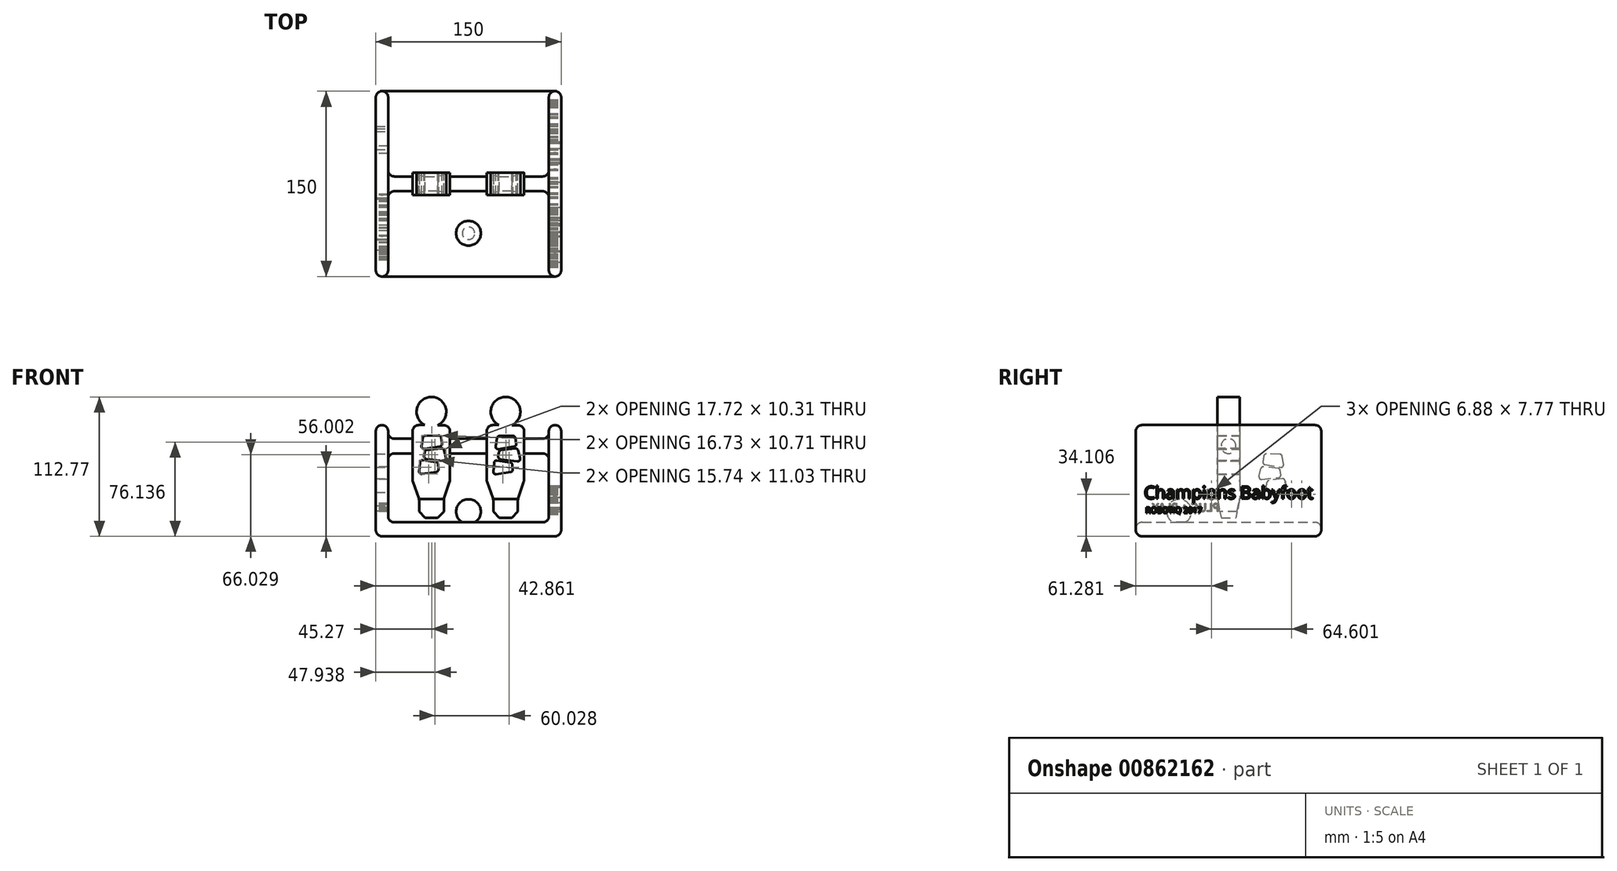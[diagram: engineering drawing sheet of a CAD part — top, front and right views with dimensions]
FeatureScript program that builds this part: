
annotation { "Feature Type Name" : "Feature", "Feature Type Description" : "" }
export const myFeature = defineFeature(function(context is Context, id is Id, definition is map)
    precondition{}
    {
        {
            var Q0;
            Q0=qCreatedBy(makeId("Front.planeOp"),FACE);
            var sketch = newSketch(context, id + "F0", { "sketchPlane" : qUnion([Q0])});
            skLineSegment(sketch, "E0.left", {"start": v(-40, 15) * mm, "end": v(-40, 0) * mm});
            skLineSegment(sketch, "E0.right", {"start": v(-20, 15) * mm, "end": v(-20, 0) * mm});
            skLineSegment(sketch, "E1", {"start": v(-45.3, 75) * mm, "end": v(-35.3, 75) * mm});
            skLineSegment(sketch, "E2", {"start": v(-25, 74.86) * mm, "end": v(-15, 74.86) * mm});
            skArc(sketch, "E3", {"start": v(-25, 74.86) * mm, "mid": v(-29.84, 97.77) * mm, "end": v(-35.3, 75) * mm});
            skLineSegment(sketch, "E4", {"start": v(-40, 0) * mm, "end": v(-30, 0) * mm});
            skLineSegment(sketch, "E5", {"start": v(-30, 0) * mm, "end": v(-20, 0) * mm});
            skLineSegment(sketch, "E6", {"start": v(-15, 74.86) * mm, "end": v(-15, 29.86) * mm});
            skLineSegment(sketch, "E7", {"start": v(-15, 29.86) * mm, "end": v(-20, 15) * mm});
            skLineSegment(sketch, "E8", {"start": v(-45.3, 75) * mm, "end": v(-45.3, 30) * mm});
            skLineSegment(sketch, "E9", {"start": v(-45.3, 30) * mm, "end": v(-40, 15) * mm});
            skLineSegment(sketch, "E10.left", {"start": v(20, 15) * mm, "end": v(20, 0) * mm});
            skLineSegment(sketch, "E10.right", {"start": v(40, 15) * mm, "end": v(40, 0) * mm});
            skLineSegment(sketch, "E11", {"start": v(14.7, 75) * mm, "end": v(24.7, 75) * mm});
            skLineSegment(sketch, "E12", {"start": v(35, 74.86) * mm, "end": v(45, 74.86) * mm});
            skArc(sketch, "E13", {"start": v(35, 74.86) * mm, "mid": v(30.16, 97.77) * mm, "end": v(24.7, 75) * mm});
            skLineSegment(sketch, "E14", {"start": v(20, 0) * mm, "end": v(30, 0) * mm});
            skLineSegment(sketch, "E15", {"start": v(30, 0) * mm, "end": v(40, 0) * mm});
            skLineSegment(sketch, "E16", {"start": v(45, 74.86) * mm, "end": v(45, 29.86) * mm});
            skLineSegment(sketch, "E17", {"start": v(45, 29.86) * mm, "end": v(40, 15) * mm});
            skLineSegment(sketch, "E18", {"start": v(14.7, 75) * mm, "end": v(14.7, 30) * mm});
            skLineSegment(sketch, "E19", {"start": v(14.7, 30) * mm, "end": v(20, 15) * mm});
            skSolve(sketch);
        }
        {
            var Q0;
            Q0=qSketchRegion(id+"F0",true);
            extrude(context, id + "F1", {"entities" : qUnion([Q0]), "endBound" : BoundingType.SYMMETRIC, "depth" : 18 * mm});
        }
        {
            var Q0;
            Q0=makeQuery(id+"F1.opExtrude","SWEPT_EDGE",EDGE,{"disambiguationData":[OSD([sQuery(id+"F0.wireOp",EDGE,"E1"),sQuery(id+"F0.wireOp",EDGE,"E8")])]});
            var Q1;
            Q1=makeQuery(id+"F1.opExtrude","SWEPT_EDGE",EDGE,{"disambiguationData":[OSD([sQuery(id+"F0.wireOp",EDGE,"E8"),sQuery(id+"F0.wireOp",EDGE,"E9")])]});
            var Q2;
            Q2=makeQuery(id+"F1.opExtrude","SWEPT_EDGE",EDGE,{"disambiguationData":[OSD([sQuery(id+"F0.wireOp",EDGE,"E0.left"),sQuery(id+"F0.wireOp",EDGE,"E9")])]});
            var Q3;
            Q3=makeQuery(id+"F1.opExtrude","SWEPT_EDGE",EDGE,{"disambiguationData":[OSD([sQuery(id+"F0.wireOp",EDGE,"E10.left"),sQuery(id+"F0.wireOp",EDGE,"E19")])]});
            var Q4;
            Q4=makeQuery(id+"F1.opExtrude","SWEPT_EDGE",EDGE,{"disambiguationData":[OSD([sQuery(id+"F0.wireOp",EDGE,"E18"),sQuery(id+"F0.wireOp",EDGE,"E19")])]});
            var Q5;
            Q5=makeQuery(id+"F1.opExtrude","SWEPT_EDGE",EDGE,{"disambiguationData":[OSD([sQuery(id+"F0.wireOp",EDGE,"E11"),sQuery(id+"F0.wireOp",EDGE,"E18")])]});
            var Q6;
            Q6=makeQuery(id+"F1.opExtrude","SWEPT_EDGE",EDGE,{"disambiguationData":[OSD([sQuery(id+"F0.wireOp",EDGE,"E2"),sQuery(id+"F0.wireOp",EDGE,"E6")])]});
            var Q7;
            Q7=makeQuery(id+"F1.opExtrude","SWEPT_EDGE",EDGE,{"disambiguationData":[OSD([sQuery(id+"F0.wireOp",EDGE,"E6"),sQuery(id+"F0.wireOp",EDGE,"E7")])]});
            var Q8;
            Q8=makeQuery(id+"F1.opExtrude","SWEPT_EDGE",EDGE,{"disambiguationData":[OSD([sQuery(id+"F0.wireOp",EDGE,"E0.right"),sQuery(id+"F0.wireOp",EDGE,"E7")])]});
            var Q9;
            Q9=makeQuery(id+"F1.opExtrude","SWEPT_EDGE",EDGE,{"disambiguationData":[OSD([sQuery(id+"F0.wireOp",EDGE,"E10.right"),sQuery(id+"F0.wireOp",EDGE,"E17")])]});
            var Q10;
            Q10=makeQuery(id+"F1.opExtrude","SWEPT_EDGE",EDGE,{"disambiguationData":[OSD([sQuery(id+"F0.wireOp",EDGE,"E16"),sQuery(id+"F0.wireOp",EDGE,"E17")])]});
            var Q11;
            Q11=makeQuery(id+"F1.opExtrude","SWEPT_EDGE",EDGE,{"disambiguationData":[OSD([sQuery(id+"F0.wireOp",EDGE,"E12"),sQuery(id+"F0.wireOp",EDGE,"E16")])]});
            fillet(context, id + "F2", {"entities" : qUnion([Q0, Q1, Q2, Q3, Q4, Q5, Q6, Q7, Q8, Q9, Q10, Q11]), "radius" : 5 * mm, "tangentPropagation" : true, "allowEdgeOverflow" : false});
        }
        {
            var Q0;
            Q0=makeQuery(id+"F1.opExtrude","SWEPT_EDGE",EDGE,{"disambiguationData":[OSD([sQuery(id+"F0.wireOp",EDGE,"E0.left"),sQuery(id+"F0.wireOp",EDGE,"E4")])]});
            var Q1;
            Q1=makeQuery(id+"F1.opExtrude","SWEPT_EDGE",EDGE,{"disambiguationData":[OSD([sQuery(id+"F0.wireOp",EDGE,"E0.right"),sQuery(id+"F0.wireOp",EDGE,"E5")])]});
            var Q2;
            Q2=makeQuery(id+"F1.opExtrude","SWEPT_EDGE",EDGE,{"disambiguationData":[OSD([sQuery(id+"F0.wireOp",EDGE,"E10.right"),sQuery(id+"F0.wireOp",EDGE,"E15")])]});
            var Q3;
            Q3=makeQuery(id+"F1.opExtrude","SWEPT_EDGE",EDGE,{"disambiguationData":[OSD([sQuery(id+"F0.wireOp",EDGE,"E10.left"),sQuery(id+"F0.wireOp",EDGE,"E14")])]});
            chamfer(context, id + "F3", {"entities" : qUnion([Q0, Q1, Q2, Q3]), "width" : 5 * mm, "tangentPropagation" : true});
        }
        {
            var Q0;
            Q0=makeQuery(id+"F1.opExtrude","CAP_EDGE",EDGE,{"disambiguationData":[OSD([sQuery(id+"F0.wireOp",EDGE,"E4"),sQuery(id+"F0.wireOp",EDGE,"E5")])],"isStart":false});
            var Q1;
            Q1=makeQuery(id+"F1.opExtrude","CAP_EDGE",EDGE,{"disambiguationData":[OSD([sQuery(id+"F0.wireOp",EDGE,"E14"),sQuery(id+"F0.wireOp",EDGE,"E15")])],"isStart":false});
            var Q2;
            Q2=makeQuery(id+"F1.opExtrude","CAP_EDGE",EDGE,{"disambiguationData":[OSD([sQuery(id+"F0.wireOp",EDGE,"E14"),sQuery(id+"F0.wireOp",EDGE,"E15")])],"isStart":true});
            var Q3;
            Q3=makeQuery(id+"F1.opExtrude","CAP_EDGE",EDGE,{"disambiguationData":[OSD([sQuery(id+"F0.wireOp",EDGE,"E4"),sQuery(id+"F0.wireOp",EDGE,"E5")])],"isStart":true});
            chamfer(context, id + "F4", {"entities" : qUnion([Q0, Q1, Q2, Q3]), "chamferType" : ChamferType.TWO_OFFSETS, "width1" : 15 * mm, "oppositeDirection" : false, "width2" : 3 * mm, "tangentPropagation" : true});
        }
        {
            var Q0;
            Q0=qCreatedBy(makeId("Right.planeOp"),FACE);
            var sketch = newSketch(context, id + "F5", { "sketchPlane" : qUnion([Q0])});
            skCircle(sketch, "E20", {"center": v(0, 58) * mm, "radius": 6 * mm});
            skSolve(sketch);
        }
        {
            var Q0;
            Q0=qSketchRegion(id+"F5",true);
            extrude(context, id + "F6", {"entities" : qUnion([Q0]), "operationType" : NewBodyOperationType.ADD, "endBound" : BoundingType.SYMMETRIC, "depth" : 150 * mm});
        }
        {
            var Q0;
            Q0=qCreatedBy(makeId("Front.planeOp"),FACE);
            cPlane(context, id + "F7", {"entities" : qUnion([Q0]), "cplaneType" : CPlaneType.OFFSET, "offset" : 40 * mm, "width" : 150 * mm, "height" : 150 * mm});
        }
        {
            var Q0;
            Q0=qCreatedBy(id+"F7.planeOp",FACE);
            var sketch = newSketch(context, id + "F8", { "sketchPlane" : qUnion([Q0])});
            skPoint(sketch, "E21", {"position": v(0, 4.98) * mm});
            skLineSegment(sketch, "E22", {"start": v(-10, 4.93) * mm, "end": v(10, 4.93) * mm});
            skArc(sketch, "E23", {"start": v(10, 4.93) * mm, "mid": v(0, 14.93) * mm, "end": v(-10, 4.93) * mm});
            skSolve(sketch);
        }
        {
            var Q0;
            Q0=qCreatedBy(makeId("Front.planeOp"),FACE);
            var sketch = newSketch(context, id + "F9", { "sketchPlane" : qUnion([Q0])});
            skLineSegment(sketch, "E24.top", {"start": v(-75, -15) * mm, "end": v(75, -15) * mm});
            skLineSegment(sketch, "E25", {"start": v(75, -15) * mm, "end": v(75, 75) * mm});
            skLineSegment(sketch, "E26", {"start": v(75, 75) * mm, "end": v(65, 75) * mm});
            skLineSegment(sketch, "E27", {"start": v(65, 75) * mm, "end": v(65, 0) * mm});
            skLineSegment(sketch, "E28", {"start": v(-65, 1.11) * mm, "end": v(-65, 75) * mm});
            skLineSegment(sketch, "E29", {"start": v(-75, -15) * mm, "end": v(-75, 75) * mm});
            skLineSegment(sketch, "E30", {"start": v(-75, 75) * mm, "end": v(-65, 75) * mm});
            skLineSegment(sketch, "E31", {"start": v(65, 0) * mm, "end": v(65, -3.72) * mm});
            skLineSegment(sketch, "E32", {"start": v(65, -3.72) * mm, "end": v(-65, -3.72) * mm});
            skLineSegment(sketch, "E33", {"start": v(-65, 1.11) * mm, "end": v(-65, -3.72) * mm});
            skSolve(sketch);
        }
        {
            var Q0;
            Q0=qSketchRegion(id+"F9",true);
            extrude(context, id + "F10", {"entities" : qUnion([Q0]), "operationType" : NewBodyOperationType.ADD, "endBound" : BoundingType.SYMMETRIC, "depth" : 150 * mm});
        }
        {
            var Q0;
            Q0=makeQuery(id+"F10.opExtrude","SWEPT_EDGE",EDGE,{"disambiguationData":[OSD([sQuery(id+"F9.wireOp",EDGE,"E29"),sQuery(id+"F9.wireOp",EDGE,"E30")])]});
            var Q1;
            Q1=makeQuery(id+"F10.opExtrude","CAP_EDGE",EDGE,{"disambiguationData":[OSD([sQuery(id+"F9.wireOp",EDGE,"E30")])],"isStart":false});
            var Q2;
            Q2=makeQuery(id+"F10.opExtrude","CAP_EDGE",EDGE,{"disambiguationData":[OSD([sQuery(id+"F9.wireOp",EDGE,"E30")])],"isStart":true});
            var Q3;
            Q3=makeQuery(id+"F10.opExtrude","SWEPT_EDGE",EDGE,{"disambiguationData":[OSD([sQuery(id+"F9.wireOp",EDGE,"E28"),sQuery(id+"F9.wireOp",EDGE,"E30")])]});
            var Q4;
            Q4=makeQuery(id+"F10.opExtrude","CAP_EDGE",EDGE,{"disambiguationData":[OSD([sQuery(id+"F9.wireOp",EDGE,"E28"),sQuery(id+"F9.wireOp",EDGE,"E33")])],"isStart":true});
            var Q5;
            Q5=makeQuery(id+"F10.opExtrude","CAP_EDGE",EDGE,{"disambiguationData":[OSD([sQuery(id+"F9.wireOp",EDGE,"E29")])],"isStart":true});
            var Q6;
            Q6=makeQuery(id+"F10.opExtrude","CAP_EDGE",EDGE,{"disambiguationData":[OSD([sQuery(id+"F9.wireOp",EDGE,"E29")])],"isStart":false});
            var Q7;
            Q7=makeQuery(id+"F10.opExtrude","CAP_EDGE",EDGE,{"disambiguationData":[OSD([sQuery(id+"F9.wireOp",EDGE,"E28"),sQuery(id+"F9.wireOp",EDGE,"E33")])],"isStart":false});
            var Q8;
            Q8=makeQuery(id+"F10.opExtrude","CAP_EDGE",EDGE,{"disambiguationData":[OSD([sQuery(id+"F9.wireOp",EDGE,"E32")])],"isStart":false});
            var Q9;
            Q9=makeQuery(id+"F10.opExtrude","CAP_EDGE",EDGE,{"disambiguationData":[OSD([sQuery(id+"F9.wireOp",EDGE,"E24.top")])],"isStart":false});
            var Q10;
            Q10=makeQuery(id+"F10.opExtrude","SWEPT_EDGE",EDGE,{"disambiguationData":[OSD([sQuery(id+"F9.wireOp",EDGE,"E24.top"),sQuery(id+"F9.wireOp",EDGE,"E29")])]});
            var Q11;
            Q11=makeQuery(id+"F10.opExtrude","CAP_EDGE",EDGE,{"disambiguationData":[OSD([sQuery(id+"F9.wireOp",EDGE,"E24.top")])],"isStart":true});
            var Q12;
            Q12=makeQuery(id+"F10.opExtrude","SWEPT_EDGE",EDGE,{"disambiguationData":[OSD([sQuery(id+"F9.wireOp",EDGE,"E24.top"),sQuery(id+"F9.wireOp",EDGE,"E25")])]});
            var Q13;
            Q13=makeQuery(id+"F10.opExtrude","CAP_EDGE",EDGE,{"disambiguationData":[OSD([sQuery(id+"F9.wireOp",EDGE,"E25")])],"isStart":false});
            var Q14;
            Q14=makeQuery(id+"F10.opExtrude","CAP_EDGE",EDGE,{"disambiguationData":[OSD([sQuery(id+"F9.wireOp",EDGE,"E27"),sQuery(id+"F9.wireOp",EDGE,"E31")])],"isStart":false});
            var Q15;
            Q15=makeQuery(id+"F10.opExtrude","CAP_EDGE",EDGE,{"disambiguationData":[OSD([sQuery(id+"F9.wireOp",EDGE,"E25")])],"isStart":true});
            var Q16;
            Q16=makeQuery(id+"F10.opExtrude","CAP_EDGE",EDGE,{"disambiguationData":[OSD([sQuery(id+"F9.wireOp",EDGE,"E27"),sQuery(id+"F9.wireOp",EDGE,"E31")])],"isStart":true});
            var Q17;
            Q17=makeQuery(id+"F10.opExtrude","CAP_EDGE",EDGE,{"disambiguationData":[OSD([sQuery(id+"F9.wireOp",EDGE,"E32")])],"isStart":true});
            var Q18;
            Q18=makeQuery(id+"F10.opExtrude","CAP_EDGE",EDGE,{"disambiguationData":[OSD([sQuery(id+"F9.wireOp",EDGE,"E26")])],"isStart":true});
            var Q19;
            Q19=makeQuery(id+"F10.opExtrude","SWEPT_EDGE",EDGE,{"disambiguationData":[OSD([sQuery(id+"F9.wireOp",EDGE,"E25"),sQuery(id+"F9.wireOp",EDGE,"E26")])]});
            var Q20;
            Q20=makeQuery(id+"F10.opExtrude","SWEPT_EDGE",EDGE,{"disambiguationData":[OSD([sQuery(id+"F9.wireOp",EDGE,"E26"),sQuery(id+"F9.wireOp",EDGE,"E27")])]});
            var Q21;
            Q21=makeQuery(id+"F10.opExtrude","SWEPT_EDGE",EDGE,{"disambiguationData":[OSD([sQuery(id+"F9.wireOp",EDGE,"E32"),sQuery(id+"F9.wireOp",EDGE,"E33")])]});
            var Q22;
            Q22=makeQuery(id+"F10.opExtrude","SWEPT_FACE",FACE,{"disambiguationData":[OSD([sQuery(id+"F9.wireOp",EDGE,"E27"),sQuery(id+"F9.wireOp",EDGE,"E31")])]});
            var Q23;
            Q23=makeQuery(id+"F10.opExtrude","CAP_EDGE",EDGE,{"disambiguationData":[OSD([sQuery(id+"F9.wireOp",EDGE,"E26")])],"isStart":false});
            var Q24;
            {var subQ0=sQuery(id+"F5.wireOp",EDGE,"E20");Q24=makeQuery(id+"F10.boolean.opBoolean","INTERSECT",EDGE,{"derivedFrom":[makeQuery(id+"F6.boolean.opBoolean","SPLIT",FACE,{"disambiguationData":[TD([makeQuery(id+"F1.opExtrude","SWEPT_FACE",FACE,{"disambiguationData":[OSD([sQuery(id+"F0.wireOp",EDGE,"E8")])]})])],"derivedFrom":makeQuery(id+"F6.opExtrude","SWEPT_FACE",FACE,{"disambiguationData":[OSD([subQ0])]})}),makeQuery(id+"F10.opExtrude","SWEPT_FACE",FACE,{"disambiguationData":[OSD([sQuery(id+"F9.wireOp",EDGE,"E28"),sQuery(id+"F9.wireOp",EDGE,"E33")])]})]});}
            fillet(context, id + "F11", {"entities" : qUnion([Q0, Q1, Q2, Q3, Q4, Q5, Q6, Q7, Q8, Q9, Q10, Q11, Q12, Q13, Q14, Q15, Q16, Q17, Q18, Q19, Q20, Q21, Q22, Q23, Q24]), "radius" : 5 * mm, "tangentPropagation" : true, "allowEdgeOverflow" : false});
        }
        {
            var Q0;
            Q0=makeQuery(id+"F10.boolean.opBoolean","MERGE",FACE,{"derivedFrom":[makeQuery(id+"F6.opExtrude","CAP_FACE",FACE,{"disambiguationData":[OSD([sQuery(id+"F5.wireOp",EDGE,"E20")])],"isStart":false}),makeQuery(id+"F10.opExtrude","SWEPT_FACE",FACE,{"disambiguationData":[OSD([sQuery(id+"F9.wireOp",EDGE,"E25")])]})]});
            var sketch = newSketch(context, id + "F12", { "sketchPlane" : qUnion([Q0])});
            skText(sketch, "E34", { "text": "Champions Babyfoot", "fontName": "OpenSans-Regular.ttf"});
            skText(sketch, "E35", { "text": "ROBOTIQ 2017", "fontName": "OpenSans-Regular.ttf"});
            const initialGuessF12  = {"E34": [-0.0683, 0.01536, 1, 0, 0.01008], "E35": [-0.06708, 0.00377, 1, 0, 0.0047]};
            skSetInitialGuess(sketch, initialGuessF12);
            skSolve(sketch);
        }
        {
            var Q0;
            Q0=qSketchRegion(id+"F12",true);
            extrude(context, id + "F13", {"entities" : qUnion([Q0]), "operationType" : NewBodyOperationType.REMOVE, "oppositeDirection" : true, "depth" : 25 * mm});
        }
        {
            var Q0;
            Q0=makeQuery(id+"F10.boolean.opBoolean","MERGE",FACE,{"derivedFrom":[makeQuery(id+"F6.opExtrude","CAP_FACE",FACE,{"disambiguationData":[OSD([sQuery(id+"F5.wireOp",EDGE,"E20")])],"isStart":true}),makeQuery(id+"F10.opExtrude","SWEPT_FACE",FACE,{"disambiguationData":[OSD([sQuery(id+"F9.wireOp",EDGE,"E29")])]})]});
            var sketch = newSketch(context, id + "F14", { "sketchPlane" : qUnion([Q0])});
            skLineSegment(sketch, "E36", {"start": v(-43.16, 51.43) * mm, "end": v(-44.96, 40.45) * mm});
            skLineSegment(sketch, "E37", {"start": v(-44.96, 40.45) * mm, "end": v(-27.5, 43.23) * mm});
            skLineSegment(sketch, "E38", {"start": v(-27.5, 43.23) * mm, "end": v(-28.84, 51.6) * mm});
            skLineSegment(sketch, "E39", {"start": v(-28.84, 51.6) * mm, "end": v(-43.16, 51.43) * mm});
            skLineSegment(sketch, "E40", {"start": v(-41.54, 39.83) * mm, "end": v(-42.66, 32.89) * mm});
            skLineSegment(sketch, "E41", {"start": v(-42.66, 32.89) * mm, "end": v(-24, 30.61) * mm});
            skLineSegment(sketch, "E42", {"start": v(-26.68, 41.46) * mm, "end": v(-41.54, 39.83) * mm});
            skLineSegment(sketch, "E43", {"start": v(-26.68, 41.46) * mm, "end": v(-24, 30.61) * mm});
            skLineSegment(sketch, "E44", {"start": v(-45.62, 31.87) * mm, "end": v(-46.67, 20.24) * mm});
            skLineSegment(sketch, "E45", {"start": v(-46.67, 20.24) * mm, "end": v(-30.53, 22.48) * mm});
            skLineSegment(sketch, "E46", {"start": v(-31.2, 29.92) * mm, "end": v(-45.62, 31.87) * mm});
            skLineSegment(sketch, "E47", {"start": v(-31.2, 29.92) * mm, "end": v(-30.53, 22.48) * mm});
            skSolve(sketch);
        }
        {
            var Q0;
            Q0=makeQuery(id+"F14.imprint","IMPRINT",FACE,{"disambiguationData":[TD([[makeQuery(id+"F14.imprint","IMPRINT",EDGE,{"derivedFrom":sQuery(id+"F14.wireOp",EDGE,"E36")}),1.0]])]});
            var Q1;
            Q1=makeQuery(id+"F14.imprint","IMPRINT",FACE,{"disambiguationData":[TD([[makeQuery(id+"F14.imprint","IMPRINT",EDGE,{"derivedFrom":sQuery(id+"F14.wireOp",EDGE,"E40")}),1.0]])]});
            var Q2;
            Q2=makeQuery(id+"F14.imprint","IMPRINT",FACE,{"disambiguationData":[TD([[makeQuery(id+"F14.imprint","IMPRINT",EDGE,{"derivedFrom":sQuery(id+"F14.wireOp",EDGE,"E44")}),1.0]])]});
            extrude(context, id + "F15", {"entities" : qUnion([Q0, Q1, Q2]), "operationType" : NewBodyOperationType.REMOVE, "oppositeDirection" : true, "depth" : 25 * mm});
        }
        {
            var Q0;
            Q0=makeQuery(id+"F15.boolean.opBoolean","COPY",EDGE,{"derivedFrom":makeQuery(id+"F15.opExtrude","SWEPT_EDGE",EDGE,{"disambiguationData":[OSD([sQuery(id+"F14.wireOp",EDGE,"E41"),sQuery(id+"F14.wireOp",EDGE,"E43")])]})});
            var Q1;
            Q1=makeQuery(id+"F15.boolean.opBoolean","COPY",EDGE,{"derivedFrom":makeQuery(id+"F15.opExtrude","SWEPT_EDGE",EDGE,{"disambiguationData":[OSD([sQuery(id+"F14.wireOp",EDGE,"E42"),sQuery(id+"F14.wireOp",EDGE,"E43")])]})});
            var Q2;
            Q2=makeQuery(id+"F15.boolean.opBoolean","COPY",EDGE,{"derivedFrom":makeQuery(id+"F15.opExtrude","SWEPT_EDGE",EDGE,{"disambiguationData":[OSD([sQuery(id+"F14.wireOp",EDGE,"E40"),sQuery(id+"F14.wireOp",EDGE,"E41")])]})});
            var Q3;
            Q3=makeQuery(id+"F15.boolean.opBoolean","COPY",EDGE,{"derivedFrom":makeQuery(id+"F15.opExtrude","SWEPT_EDGE",EDGE,{"disambiguationData":[OSD([sQuery(id+"F14.wireOp",EDGE,"E40"),sQuery(id+"F14.wireOp",EDGE,"E42")])]})});
            var Q4;
            Q4=makeQuery(id+"F15.boolean.opBoolean","COPY",EDGE,{"derivedFrom":makeQuery(id+"F15.opExtrude","SWEPT_EDGE",EDGE,{"disambiguationData":[OSD([sQuery(id+"F14.wireOp",EDGE,"E44"),sQuery(id+"F14.wireOp",EDGE,"E46")])]})});
            var Q5;
            Q5=makeQuery(id+"F15.boolean.opBoolean","COPY",EDGE,{"derivedFrom":makeQuery(id+"F15.opExtrude","SWEPT_EDGE",EDGE,{"disambiguationData":[OSD([sQuery(id+"F14.wireOp",EDGE,"E46"),sQuery(id+"F14.wireOp",EDGE,"E47")])]})});
            var Q6;
            Q6=makeQuery(id+"F15.boolean.opBoolean","COPY",EDGE,{"derivedFrom":makeQuery(id+"F15.opExtrude","SWEPT_EDGE",EDGE,{"disambiguationData":[OSD([sQuery(id+"F14.wireOp",EDGE,"E45"),sQuery(id+"F14.wireOp",EDGE,"E47")])]})});
            var Q7;
            Q7=makeQuery(id+"F15.boolean.opBoolean","COPY",EDGE,{"derivedFrom":makeQuery(id+"F15.opExtrude","SWEPT_EDGE",EDGE,{"disambiguationData":[OSD([sQuery(id+"F14.wireOp",EDGE,"E44"),sQuery(id+"F14.wireOp",EDGE,"E45")])]})});
            var Q8;
            Q8=makeQuery(id+"F15.boolean.opBoolean","COPY",EDGE,{"derivedFrom":makeQuery(id+"F15.opExtrude","SWEPT_EDGE",EDGE,{"disambiguationData":[OSD([sQuery(id+"F14.wireOp",EDGE,"E37"),sQuery(id+"F14.wireOp",EDGE,"E38")])]})});
            var Q9;
            Q9=makeQuery(id+"F15.boolean.opBoolean","COPY",EDGE,{"derivedFrom":makeQuery(id+"F15.opExtrude","SWEPT_EDGE",EDGE,{"disambiguationData":[OSD([sQuery(id+"F14.wireOp",EDGE,"E38"),sQuery(id+"F14.wireOp",EDGE,"E39")])]})});
            var Q10;
            Q10=makeQuery(id+"F15.boolean.opBoolean","COPY",EDGE,{"derivedFrom":makeQuery(id+"F15.opExtrude","SWEPT_EDGE",EDGE,{"disambiguationData":[OSD([sQuery(id+"F14.wireOp",EDGE,"E36"),sQuery(id+"F14.wireOp",EDGE,"E37")])]})});
            var Q11;
            Q11=makeQuery(id+"F15.boolean.opBoolean","COPY",EDGE,{"derivedFrom":makeQuery(id+"F15.opExtrude","SWEPT_EDGE",EDGE,{"disambiguationData":[OSD([sQuery(id+"F14.wireOp",EDGE,"E36"),sQuery(id+"F14.wireOp",EDGE,"E39")])]})});
            fillet(context, id + "F16", {"entities" : qUnion([Q0, Q1, Q2, Q3, Q4, Q5, Q6, Q7, Q8, Q9, Q10, Q11]), "radius" : 2 * mm, "tangentPropagation" : true, "allowEdgeOverflow" : false});
        }
        {
            var Q0;
            Q0=makeQuery(id+"F1.opExtrude","CAP_FACE",FACE,{"disambiguationData":[OSD([sQuery(id+"F0.wireOp",EDGE,"E0.left"),sQuery(id+"F0.wireOp",EDGE,"E0.right"),sQuery(id+"F0.wireOp",EDGE,"E1"),sQuery(id+"F0.wireOp",EDGE,"E2"),sQuery(id+"F0.wireOp",EDGE,"E3"),sQuery(id+"F0.wireOp",EDGE,"E4"),sQuery(id+"F0.wireOp",EDGE,"E5"),sQuery(id+"F0.wireOp",EDGE,"E6"),sQuery(id+"F0.wireOp",EDGE,"E7"),sQuery(id+"F0.wireOp",EDGE,"E8"),sQuery(id+"F0.wireOp",EDGE,"E9")])],"isStart":false});
            var sketch = newSketch(context, id + "F17", { "sketchPlane" : qUnion([Q0])});
            skLineSegment(sketch, "E48", {"start": v(-36.73, 66.34) * mm, "end": v(-38.52, 55.37) * mm});
            skLineSegment(sketch, "E49", {"start": v(-38.52, 55.37) * mm, "end": v(-21.07, 58.15) * mm});
            skLineSegment(sketch, "E50", {"start": v(-21.07, 58.15) * mm, "end": v(-22.4, 66.51) * mm});
            skLineSegment(sketch, "E51", {"start": v(-22.4, 66.51) * mm, "end": v(-36.73, 66.34) * mm});
            skLineSegment(sketch, "E52", {"start": v(-35.11, 54.74) * mm, "end": v(-36.23, 47.8) * mm});
            skLineSegment(sketch, "E53", {"start": v(-36.23, 47.8) * mm, "end": v(-17.56, 45.52) * mm});
            skLineSegment(sketch, "E54", {"start": v(-20.25, 56.37) * mm, "end": v(-35.11, 54.74) * mm});
            skLineSegment(sketch, "E55", {"start": v(-20.25, 56.37) * mm, "end": v(-17.56, 45.52) * mm});
            skLineSegment(sketch, "E56", {"start": v(-39.18, 46.78) * mm, "end": v(-40.24, 35.15) * mm});
            skLineSegment(sketch, "E57", {"start": v(-40.24, 35.15) * mm, "end": v(-24.1, 37.4) * mm});
            skLineSegment(sketch, "E58", {"start": v(-24.78, 44.83) * mm, "end": v(-39.18, 46.78) * mm});
            skLineSegment(sketch, "E59", {"start": v(-24.78, 44.83) * mm, "end": v(-24.1, 37.4) * mm});
            skLineSegment(sketch, "E60", {"start": v(23.3, 66.12) * mm, "end": v(21.5, 55.15) * mm});
            skLineSegment(sketch, "E61", {"start": v(21.5, 55.15) * mm, "end": v(38.96, 57.93) * mm});
            skLineSegment(sketch, "E62", {"start": v(38.96, 57.93) * mm, "end": v(37.62, 66.3) * mm});
            skLineSegment(sketch, "E63", {"start": v(37.62, 66.3) * mm, "end": v(23.3, 66.12) * mm});
            skLineSegment(sketch, "E64", {"start": v(24.92, 54.52) * mm, "end": v(23.8, 47.58) * mm});
            skLineSegment(sketch, "E65", {"start": v(23.8, 47.58) * mm, "end": v(42.47, 45.3) * mm});
            skLineSegment(sketch, "E66", {"start": v(39.78, 56.15) * mm, "end": v(24.92, 54.52) * mm});
            skLineSegment(sketch, "E67", {"start": v(39.78, 56.15) * mm, "end": v(42.47, 45.3) * mm});
            skLineSegment(sketch, "E68", {"start": v(20.84, 46.56) * mm, "end": v(19.8, 34.93) * mm});
            skLineSegment(sketch, "E69", {"start": v(19.8, 34.93) * mm, "end": v(35.93, 37.17) * mm});
            skLineSegment(sketch, "E70", {"start": v(35.25, 44.6) * mm, "end": v(20.84, 46.56) * mm});
            skLineSegment(sketch, "E71", {"start": v(35.25, 44.6) * mm, "end": v(35.93, 37.17) * mm});
            skSolve(sketch);
        }
        {
            var Q0;
            Q0=qSketchRegion(id+"F17",true);
            extrude(context, id + "F18", {"entities" : qUnion([Q0]), "operationType" : NewBodyOperationType.REMOVE, "oppositeDirection" : true, "depth" : 25 * mm});
        }
        {
            var Q0;
            Q0=makeQuery(id+"F18.boolean.opBoolean","COPY",EDGE,{"derivedFrom":makeQuery(id+"F18.opExtrude","SWEPT_EDGE",EDGE,{"disambiguationData":[OSD([sQuery(id+"F17.wireOp",EDGE,"E48"),sQuery(id+"F17.wireOp",EDGE,"E51")])]})});
            var Q1;
            Q1=makeQuery(id+"F18.boolean.opBoolean","COPY",EDGE,{"derivedFrom":makeQuery(id+"F18.opExtrude","SWEPT_EDGE",EDGE,{"disambiguationData":[OSD([sQuery(id+"F17.wireOp",EDGE,"E52"),sQuery(id+"F17.wireOp",EDGE,"E54")])]})});
            var Q2;
            Q2=makeQuery(id+"F18.boolean.opBoolean","COPY",EDGE,{"derivedFrom":makeQuery(id+"F18.opExtrude","SWEPT_EDGE",EDGE,{"disambiguationData":[OSD([sQuery(id+"F17.wireOp",EDGE,"E56"),sQuery(id+"F17.wireOp",EDGE,"E58")])]})});
            var Q3;
            Q3=makeQuery(id+"F18.boolean.opBoolean","COPY",EDGE,{"derivedFrom":makeQuery(id+"F18.opExtrude","SWEPT_EDGE",EDGE,{"disambiguationData":[OSD([sQuery(id+"F17.wireOp",EDGE,"E50"),sQuery(id+"F17.wireOp",EDGE,"E51")])]})});
            var Q4;
            Q4=makeQuery(id+"F18.boolean.opBoolean","COPY",EDGE,{"derivedFrom":makeQuery(id+"F18.opExtrude","SWEPT_EDGE",EDGE,{"disambiguationData":[OSD([sQuery(id+"F17.wireOp",EDGE,"E54"),sQuery(id+"F17.wireOp",EDGE,"E55")])]})});
            var Q5;
            Q5=makeQuery(id+"F18.boolean.opBoolean","COPY",EDGE,{"derivedFrom":makeQuery(id+"F18.opExtrude","SWEPT_EDGE",EDGE,{"disambiguationData":[OSD([sQuery(id+"F17.wireOp",EDGE,"E58"),sQuery(id+"F17.wireOp",EDGE,"E59")])]})});
            var Q6;
            Q6=makeQuery(id+"F18.boolean.opBoolean","COPY",EDGE,{"derivedFrom":makeQuery(id+"F18.opExtrude","SWEPT_EDGE",EDGE,{"disambiguationData":[OSD([sQuery(id+"F17.wireOp",EDGE,"E70"),sQuery(id+"F17.wireOp",EDGE,"E71")])]})});
            var Q7;
            Q7=makeQuery(id+"F18.boolean.opBoolean","COPY",EDGE,{"derivedFrom":makeQuery(id+"F18.opExtrude","SWEPT_EDGE",EDGE,{"disambiguationData":[OSD([sQuery(id+"F17.wireOp",EDGE,"E66"),sQuery(id+"F17.wireOp",EDGE,"E67")])]})});
            var Q8;
            Q8=makeQuery(id+"F18.boolean.opBoolean","COPY",EDGE,{"derivedFrom":makeQuery(id+"F18.opExtrude","SWEPT_EDGE",EDGE,{"disambiguationData":[OSD([sQuery(id+"F17.wireOp",EDGE,"E62"),sQuery(id+"F17.wireOp",EDGE,"E63")])]})});
            var Q9;
            Q9=makeQuery(id+"F18.boolean.opBoolean","COPY",EDGE,{"derivedFrom":makeQuery(id+"F18.opExtrude","SWEPT_EDGE",EDGE,{"disambiguationData":[OSD([sQuery(id+"F17.wireOp",EDGE,"E68"),sQuery(id+"F17.wireOp",EDGE,"E70")])]})});
            var Q10;
            Q10=makeQuery(id+"F18.boolean.opBoolean","COPY",EDGE,{"derivedFrom":makeQuery(id+"F18.opExtrude","SWEPT_EDGE",EDGE,{"disambiguationData":[OSD([sQuery(id+"F17.wireOp",EDGE,"E64"),sQuery(id+"F17.wireOp",EDGE,"E66")])]})});
            var Q11;
            Q11=makeQuery(id+"F18.boolean.opBoolean","COPY",EDGE,{"derivedFrom":makeQuery(id+"F18.opExtrude","SWEPT_EDGE",EDGE,{"disambiguationData":[OSD([sQuery(id+"F17.wireOp",EDGE,"E60"),sQuery(id+"F17.wireOp",EDGE,"E63")])]})});
            var Q12;
            Q12=makeQuery(id+"F18.boolean.opBoolean","COPY",EDGE,{"derivedFrom":makeQuery(id+"F18.opExtrude","SWEPT_EDGE",EDGE,{"disambiguationData":[OSD([sQuery(id+"F17.wireOp",EDGE,"E68"),sQuery(id+"F17.wireOp",EDGE,"E69")])]})});
            var Q13;
            Q13=makeQuery(id+"F18.boolean.opBoolean","COPY",EDGE,{"derivedFrom":makeQuery(id+"F18.opExtrude","SWEPT_EDGE",EDGE,{"disambiguationData":[OSD([sQuery(id+"F17.wireOp",EDGE,"E64"),sQuery(id+"F17.wireOp",EDGE,"E65")])]})});
            var Q14;
            Q14=makeQuery(id+"F18.boolean.opBoolean","COPY",EDGE,{"derivedFrom":makeQuery(id+"F18.opExtrude","SWEPT_EDGE",EDGE,{"disambiguationData":[OSD([sQuery(id+"F17.wireOp",EDGE,"E60"),sQuery(id+"F17.wireOp",EDGE,"E61")])]})});
            var Q15;
            Q15=makeQuery(id+"F18.boolean.opBoolean","COPY",EDGE,{"derivedFrom":makeQuery(id+"F18.opExtrude","SWEPT_EDGE",EDGE,{"disambiguationData":[OSD([sQuery(id+"F17.wireOp",EDGE,"E52"),sQuery(id+"F17.wireOp",EDGE,"E53")])]})});
            var Q16;
            Q16=makeQuery(id+"F18.boolean.opBoolean","COPY",EDGE,{"derivedFrom":makeQuery(id+"F18.opExtrude","SWEPT_EDGE",EDGE,{"disambiguationData":[OSD([sQuery(id+"F17.wireOp",EDGE,"E56"),sQuery(id+"F17.wireOp",EDGE,"E57")])]})});
            var Q17;
            Q17=makeQuery(id+"F18.boolean.opBoolean","COPY",EDGE,{"derivedFrom":makeQuery(id+"F18.opExtrude","SWEPT_EDGE",EDGE,{"disambiguationData":[OSD([sQuery(id+"F17.wireOp",EDGE,"E48"),sQuery(id+"F17.wireOp",EDGE,"E49")])]})});
            var Q18;
            Q18=makeQuery(id+"F18.boolean.opBoolean","COPY",EDGE,{"derivedFrom":makeQuery(id+"F18.opExtrude","SWEPT_EDGE",EDGE,{"disambiguationData":[OSD([sQuery(id+"F17.wireOp",EDGE,"E49"),sQuery(id+"F17.wireOp",EDGE,"E50")])]})});
            var Q19;
            Q19=makeQuery(id+"F18.boolean.opBoolean","COPY",EDGE,{"derivedFrom":makeQuery(id+"F18.opExtrude","SWEPT_EDGE",EDGE,{"disambiguationData":[OSD([sQuery(id+"F17.wireOp",EDGE,"E53"),sQuery(id+"F17.wireOp",EDGE,"E55")])]})});
            var Q20;
            Q20=makeQuery(id+"F18.boolean.opBoolean","COPY",EDGE,{"derivedFrom":makeQuery(id+"F18.opExtrude","SWEPT_EDGE",EDGE,{"disambiguationData":[OSD([sQuery(id+"F17.wireOp",EDGE,"E57"),sQuery(id+"F17.wireOp",EDGE,"E59")])]})});
            var Q21;
            Q21=makeQuery(id+"F18.boolean.opBoolean","COPY",EDGE,{"derivedFrom":makeQuery(id+"F18.opExtrude","SWEPT_EDGE",EDGE,{"disambiguationData":[OSD([sQuery(id+"F17.wireOp",EDGE,"E69"),sQuery(id+"F17.wireOp",EDGE,"E71")])]})});
            var Q22;
            Q22=makeQuery(id+"F18.boolean.opBoolean","COPY",EDGE,{"derivedFrom":makeQuery(id+"F18.opExtrude","SWEPT_EDGE",EDGE,{"disambiguationData":[OSD([sQuery(id+"F17.wireOp",EDGE,"E65"),sQuery(id+"F17.wireOp",EDGE,"E67")])]})});
            var Q23;
            Q23=makeQuery(id+"F18.boolean.opBoolean","COPY",EDGE,{"derivedFrom":makeQuery(id+"F18.opExtrude","SWEPT_EDGE",EDGE,{"disambiguationData":[OSD([sQuery(id+"F17.wireOp",EDGE,"E61"),sQuery(id+"F17.wireOp",EDGE,"E62")])]})});
            fillet(context, id + "F19", {"entities" : qUnion([Q0, Q1, Q2, Q3, Q4, Q5, Q6, Q7, Q8, Q9, Q10, Q11, Q12, Q13, Q14, Q15, Q16, Q17, Q18, Q19, Q20, Q21, Q22, Q23]), "radius" : 2 * mm, "tangentPropagation" : true, "allowEdgeOverflow" : false});
        }
        {
            var Q0;
            Q0=makeQuery(id+"F10.boolean.opBoolean","MERGE",FACE,{"derivedFrom":[makeQuery(id+"F6.opExtrude","CAP_FACE",FACE,{"disambiguationData":[OSD([sQuery(id+"F5.wireOp",EDGE,"E20")])],"isStart":true}),makeQuery(id+"F10.opExtrude","SWEPT_FACE",FACE,{"disambiguationData":[OSD([sQuery(id+"F9.wireOp",EDGE,"E29")])]})]});
            var sketch = newSketch(context, id + "F20", { "sketchPlane" : qUnion([Q0])});
            skText(sketch, "E72", { "text": "PLUG + PLAY", "fontName": "OpenSans-Regular.ttf"});
            const initialGuessF20  = {"E72": [0.00746, 0.00511, 1, 0, 0.00653]};
            skSetInitialGuess(sketch, initialGuessF20);
            skSolve(sketch);
        }
        {
            var Q0;
            Q0=qSketchRegion(id+"F20",true);
            extrude(context, id + "F21", {"entities" : qUnion([Q0]), "operationType" : NewBodyOperationType.REMOVE, "oppositeDirection" : true, "depth" : 25 * mm});
        }
        {
            var Q0;
            Q0=makeQuery(id+"F8.imprint","IMPRINT",FACE,{"disambiguationData":[TD([[makeQuery(id+"F8.imprint","IMPRINT",EDGE,{"derivedFrom":sQuery(id+"F8.wireOp",EDGE,"E22")}),1.0]])]});
            var Q1;
            Q1=sQuery(id+"F8.wireOp",EDGE,"E23");
            var Q2;
            Q2=sQuery(id+"F8.wireOp",EDGE,"E22");
            revolve(context, id + "F22", {"operationType" : NewBodyOperationType.ADD, "entities" : qUnion([Q0]), "surfaceEntities" : qUnion([Q1]), "axis" : qUnion([Q2]), "revolveType" : RevolveType.FULL});
        }
        {
            var Q0;
            {var subQ1=sQuery(id+"F9.wireOp",EDGE,"E25");Q0=makeQuery(id+"F13.boolean.opBoolean","SPLIT",FACE,{"disambiguationData":[TD([makeQuery(id+"F13.opExtrude","SWEPT_FACE",FACE,{"disambiguationData":[OSD([sQuery(id+"F12.wireOp",EDGE,"E34.sketch_text.stroke-0")])]})])],"derivedFrom":makeQuery(id+"F10.boolean.opBoolean","MERGE",FACE,{"derivedFrom":[makeQuery(id+"F6.opExtrude","CAP_FACE",FACE,{"disambiguationData":[OSD([sQuery(id+"F5.wireOp",EDGE,"E20")])],"isStart":false}),makeQuery(id+"F10.opExtrude","SWEPT_FACE",FACE,{"disambiguationData":[OSD([subQ1])]})]})});}
            cPlane(context, id + "F23", {"entities" : qUnion([Q0]), "cplaneType" : CPlaneType.OFFSET, "offset" : 5 * mm, "oppositeDirection" : true, "width" : 150 * mm, "height" : 150 * mm});
        }
        {
            var Q0;
            Q0=qCreatedBy(id+"F23.planeOp",FACE);
            var sketch = newSketch(context, id + "F24", { "sketchPlane" : qUnion([Q0])});
            skLineSegment(sketch, "E73.bottom", {"start": v(-51, 18.05) * mm, "end": v(-42.89, 18.05) * mm});
            skLineSegment(sketch, "E73.top", {"start": v(-51, 17.68) * mm, "end": v(-42.89, 17.68) * mm});
            skLineSegment(sketch, "E73.left", {"start": v(-51, 18.05) * mm, "end": v(-51, 17.68) * mm});
            skLineSegment(sketch, "E73.right", {"start": v(-42.89, 18.05) * mm, "end": v(-42.89, 17.68) * mm});
            skLineSegment(sketch, "E74.bottom", {"start": v(-29.8, 19.6) * mm, "end": v(-21.69, 19.6) * mm});
            skLineSegment(sketch, "E74.top", {"start": v(-29.8, 19.24) * mm, "end": v(-21.69, 19.24) * mm});
            skLineSegment(sketch, "E74.left", {"start": v(-29.8, 19.6) * mm, "end": v(-29.8, 19.24) * mm});
            skLineSegment(sketch, "E74.right", {"start": v(-21.69, 19.6) * mm, "end": v(-21.69, 19.24) * mm});
            skLineSegment(sketch, "E75.bottom", {"start": v(-17.86, 18.85) * mm, "end": v(-9.76, 18.85) * mm});
            skLineSegment(sketch, "E75.top", {"start": v(-17.86, 18.49) * mm, "end": v(-9.76, 18.49) * mm});
            skLineSegment(sketch, "E75.left", {"start": v(-17.86, 18.85) * mm, "end": v(-17.86, 18.49) * mm});
            skLineSegment(sketch, "E75.right", {"start": v(-9.76, 18.85) * mm, "end": v(-9.76, 18.49) * mm});
            skLineSegment(sketch, "E76.bottom", {"start": v(18.43, 17.76) * mm, "end": v(26.53, 17.76) * mm});
            skLineSegment(sketch, "E76.top", {"start": v(18.43, 17.4) * mm, "end": v(26.53, 17.4) * mm});
            skLineSegment(sketch, "E76.left", {"start": v(18.43, 17.76) * mm, "end": v(18.43, 17.4) * mm});
            skLineSegment(sketch, "E76.right", {"start": v(26.53, 17.76) * mm, "end": v(26.53, 17.4) * mm});
            skLineSegment(sketch, "E77.bottom", {"start": v(46.91, 19) * mm, "end": v(55.02, 19) * mm});
            skLineSegment(sketch, "E77.top", {"start": v(46.91, 18.64) * mm, "end": v(55.02, 18.64) * mm});
            skLineSegment(sketch, "E77.left", {"start": v(46.91, 19) * mm, "end": v(46.91, 18.64) * mm});
            skLineSegment(sketch, "E77.right", {"start": v(55.02, 19) * mm, "end": v(55.02, 18.64) * mm});
            skLineSegment(sketch, "E78.bottom", {"start": v(55.52, 19) * mm, "end": v(63.62, 19) * mm});
            skLineSegment(sketch, "E78.top", {"start": v(55.52, 18.64) * mm, "end": v(63.62, 18.64) * mm});
            skLineSegment(sketch, "E78.left", {"start": v(55.52, 19) * mm, "end": v(55.52, 18.64) * mm});
            skLineSegment(sketch, "E78.right", {"start": v(63.62, 19) * mm, "end": v(63.62, 18.64) * mm});
            skLineSegment(sketch, "E79.bottom", {"start": v(26.5, 19.25) * mm, "end": v(34.6, 19.25) * mm});
            skLineSegment(sketch, "E79.top", {"start": v(26.5, 18.89) * mm, "end": v(34.6, 18.89) * mm});
            skLineSegment(sketch, "E79.left", {"start": v(26.5, 19.25) * mm, "end": v(26.5, 18.89) * mm});
            skLineSegment(sketch, "E79.right", {"start": v(34.6, 19.25) * mm, "end": v(34.6, 18.89) * mm});
            skLineSegment(sketch, "E80.bottom", {"start": v(9.9, 18.27) * mm, "end": v(18, 18.27) * mm});
            skLineSegment(sketch, "E80.top", {"start": v(9.9, 17.9) * mm, "end": v(18, 17.9) * mm});
            skLineSegment(sketch, "E80.left", {"start": v(9.9, 18.27) * mm, "end": v(9.9, 17.9) * mm});
            skLineSegment(sketch, "E80.right", {"start": v(18, 18.27) * mm, "end": v(18, 17.9) * mm});
            skLineSegment(sketch, "E81.bottom", {"start": v(10.2, 22.86) * mm, "end": v(18.3, 22.86) * mm});
            skLineSegment(sketch, "E81.top", {"start": v(10.2, 22.5) * mm, "end": v(18.3, 22.5) * mm});
            skLineSegment(sketch, "E81.left", {"start": v(10.2, 22.86) * mm, "end": v(10.2, 22.5) * mm});
            skLineSegment(sketch, "E81.right", {"start": v(18.3, 22.86) * mm, "end": v(18.3, 22.5) * mm});
            skLineSegment(sketch, "E82.bottom", {"start": v(-62.99, 5.84) * mm, "end": v(-57.87, 5.84) * mm});
            skLineSegment(sketch, "E82.top", {"start": v(-62.99, 5.42) * mm, "end": v(-57.87, 5.42) * mm});
            skLineSegment(sketch, "E82.left", {"start": v(-62.99, 5.84) * mm, "end": v(-62.99, 5.42) * mm});
            skLineSegment(sketch, "E82.right", {"start": v(-57.87, 5.84) * mm, "end": v(-57.87, 5.42) * mm});
            skLineSegment(sketch, "E83.bottom", {"start": v(-58.13, 5.13) * mm, "end": v(-53.02, 5.13) * mm});
            skLineSegment(sketch, "E83.top", {"start": v(-58.13, 4.7) * mm, "end": v(-53.02, 4.7) * mm});
            skLineSegment(sketch, "E83.left", {"start": v(-58.13, 5.13) * mm, "end": v(-58.13, 4.7) * mm});
            skLineSegment(sketch, "E83.right", {"start": v(-53.02, 5.13) * mm, "end": v(-53.02, 4.7) * mm});
            skLineSegment(sketch, "E84.bottom", {"start": v(-58.45, 7.86) * mm, "end": v(-53.34, 7.86) * mm});
            skLineSegment(sketch, "E84.top", {"start": v(-58.45, 7.44) * mm, "end": v(-53.34, 7.44) * mm});
            skLineSegment(sketch, "E84.left", {"start": v(-58.45, 7.86) * mm, "end": v(-58.45, 7.44) * mm});
            skLineSegment(sketch, "E84.right", {"start": v(-53.34, 7.86) * mm, "end": v(-53.34, 7.44) * mm});
            skLineSegment(sketch, "E85.bottom", {"start": v(-53.91, 6.58) * mm, "end": v(-48.8, 6.58) * mm});
            skLineSegment(sketch, "E85.top", {"start": v(-53.91, 6.16) * mm, "end": v(-48.8, 6.16) * mm});
            skLineSegment(sketch, "E85.left", {"start": v(-53.91, 6.58) * mm, "end": v(-53.91, 6.16) * mm});
            skLineSegment(sketch, "E85.right", {"start": v(-48.8, 6.58) * mm, "end": v(-48.8, 6.16) * mm});
            skLineSegment(sketch, "E86.bottom", {"start": v(-67.86, 7.52) * mm, "end": v(-62.75, 7.52) * mm});
            skLineSegment(sketch, "E86.top", {"start": v(-67.86, 7.1) * mm, "end": v(-62.75, 7.1) * mm});
            skLineSegment(sketch, "E86.left", {"start": v(-67.86, 7.52) * mm, "end": v(-67.86, 7.1) * mm});
            skLineSegment(sketch, "E86.right", {"start": v(-62.75, 7.52) * mm, "end": v(-62.75, 7.1) * mm});
            skLineSegment(sketch, "E87.bottom", {"start": v(-43.36, 6.3) * mm, "end": v(-38.25, 6.3) * mm});
            skLineSegment(sketch, "E87.top", {"start": v(-43.36, 5.87) * mm, "end": v(-38.25, 5.87) * mm});
            skLineSegment(sketch, "E87.left", {"start": v(-43.36, 6.3) * mm, "end": v(-43.36, 5.87) * mm});
            skLineSegment(sketch, "E87.right", {"start": v(-38.25, 6.3) * mm, "end": v(-38.25, 5.87) * mm});
            skLineSegment(sketch, "E88.bottom", {"start": v(-33.15, 6.13) * mm, "end": v(-28.04, 6.13) * mm});
            skLineSegment(sketch, "E88.top", {"start": v(-33.15, 5.7) * mm, "end": v(-28.04, 5.7) * mm});
            skLineSegment(sketch, "E88.left", {"start": v(-33.15, 6.13) * mm, "end": v(-33.15, 5.7) * mm});
            skLineSegment(sketch, "E88.right", {"start": v(-28.04, 6.13) * mm, "end": v(-28.04, 5.7) * mm});
            skSolve(sketch);
        }
        {
            var Q0;
            Q0=qSketchRegion(id+"F24",true);
            extrude(context, id + "F25", {"entities" : qUnion([Q0]), "operationType" : NewBodyOperationType.ADD, "endBound" : BoundingType.SYMMETRIC, "depth" : 2 * mm});
        }
        {
            var Q0;
            {var subQ0=sQuery(id+"F9.wireOp",EDGE,"E29");var subQ3=sQuery(id+"F14.wireOp",EDGE,"E36");Q0=makeQuery(id+"F21.boolean.opBoolean","SPLIT",FACE,{"disambiguationData":[TD([makeQuery(id+"F15.boolean.opBoolean","COPY",FACE,{"derivedFrom":makeQuery(id+"F15.opExtrude","SWEPT_FACE",FACE,{"disambiguationData":[OSD([subQ3])]})})])],"derivedFrom":makeQuery(id+"F10.boolean.opBoolean","MERGE",FACE,{"derivedFrom":[makeQuery(id+"F6.opExtrude","CAP_FACE",FACE,{"disambiguationData":[OSD([sQuery(id+"F5.wireOp",EDGE,"E20")])],"isStart":true}),makeQuery(id+"F10.opExtrude","SWEPT_FACE",FACE,{"disambiguationData":[OSD([subQ0])]})]})});}
            cPlane(context, id + "F26", {"entities" : qUnion([Q0]), "cplaneType" : CPlaneType.OFFSET, "offset" : 5 * mm, "oppositeDirection" : true, "width" : 150 * mm, "height" : 150 * mm});
        }
        {
            var Q0;
            Q0=qCreatedBy(id+"F26.planeOp",FACE);
            var sketch = newSketch(context, id + "F27", { "sketchPlane" : qUnion([Q0])});
            skLineSegment(sketch, "E89.bottom", {"start": v(6.92, 9.94) * mm, "end": v(13.12, 9.94) * mm});
            skLineSegment(sketch, "E89.top", {"start": v(6.92, 9.23) * mm, "end": v(13.12, 9.23) * mm});
            skLineSegment(sketch, "E89.left", {"start": v(6.92, 9.94) * mm, "end": v(6.92, 9.23) * mm});
            skLineSegment(sketch, "E89.right", {"start": v(13.12, 9.94) * mm, "end": v(13.12, 9.23) * mm});
            skLineSegment(sketch, "E90.bottom", {"start": v(41, 9.83) * mm, "end": v(46.31, 9.83) * mm});
            skLineSegment(sketch, "E90.top", {"start": v(41, 9.23) * mm, "end": v(46.31, 9.23) * mm});
            skLineSegment(sketch, "E90.left", {"start": v(41, 9.83) * mm, "end": v(41, 9.23) * mm});
            skLineSegment(sketch, "E90.right", {"start": v(46.31, 9.83) * mm, "end": v(46.31, 9.23) * mm});
            skLineSegment(sketch, "E91.bottom", {"start": v(51.55, 9.83) * mm, "end": v(55.96, 9.83) * mm});
            skLineSegment(sketch, "E91.top", {"start": v(51.55, 9.23) * mm, "end": v(55.96, 9.23) * mm});
            skLineSegment(sketch, "E91.left", {"start": v(51.55, 9.83) * mm, "end": v(51.55, 9.23) * mm});
            skLineSegment(sketch, "E91.right", {"start": v(55.96, 9.83) * mm, "end": v(55.96, 9.23) * mm});
            skSolve(sketch);
        }
        {
            var Q0;
            Q0=qSketchRegion(id+"F27",true);
            extrude(context, id + "F28", {"entities" : qUnion([Q0]), "operationType" : NewBodyOperationType.ADD, "endBound" : BoundingType.SYMMETRIC, "depth" : 2 * mm});
        }
    });
